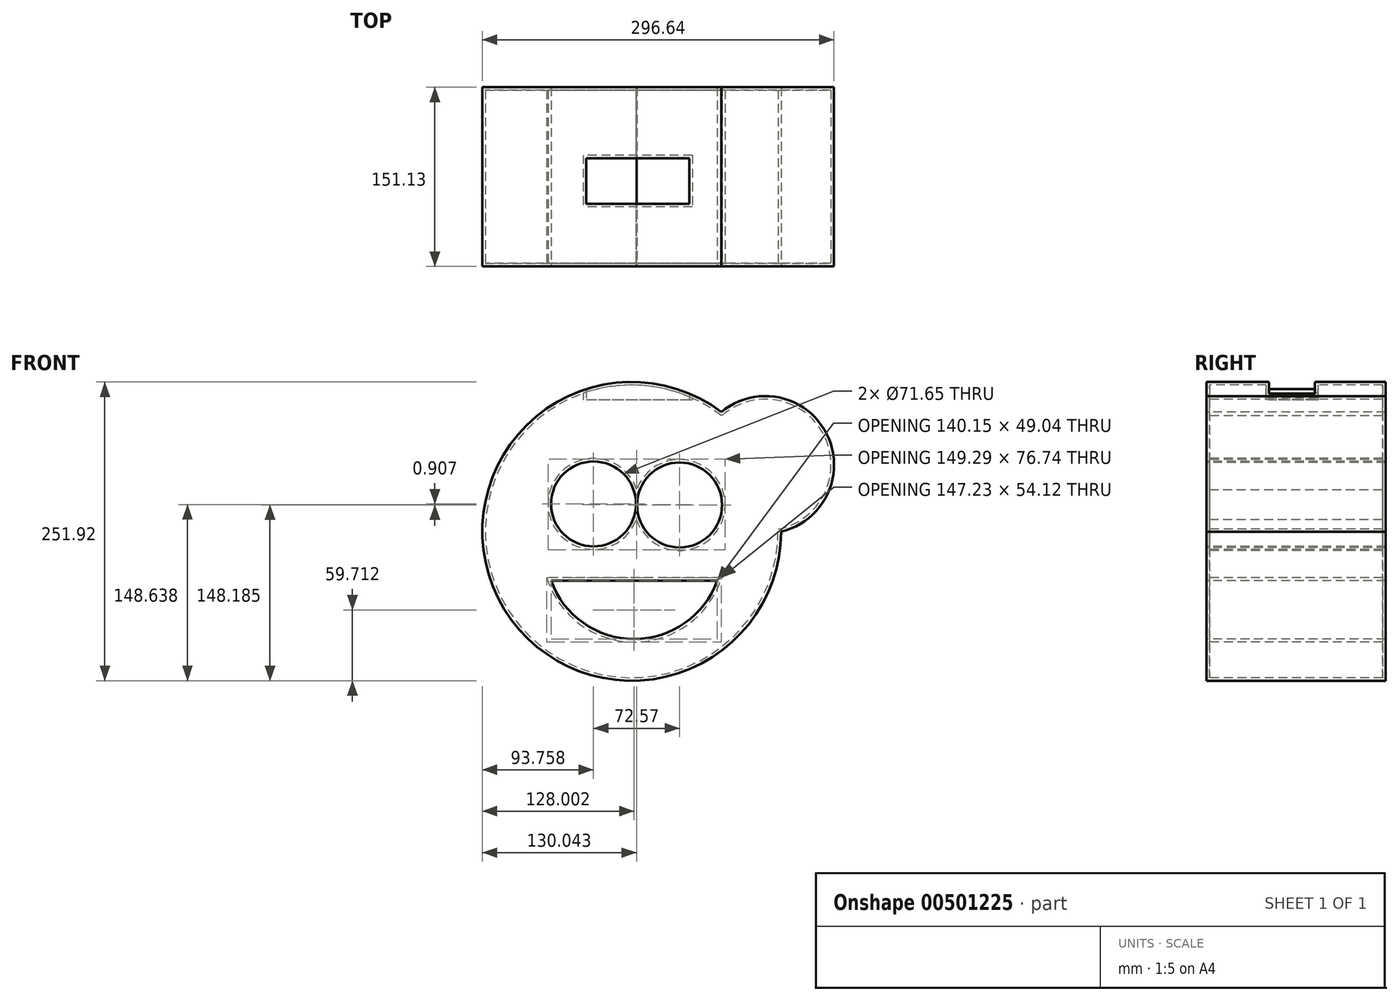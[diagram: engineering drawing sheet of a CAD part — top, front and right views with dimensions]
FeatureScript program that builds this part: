
annotation { "Feature Type Name" : "Feature", "Feature Type Description" : "" }
export const myFeature = defineFeature(function(context is Context, id is Id, definition is map)
    precondition{}
    {
        {
            var Q0;
            Q0=qCreatedBy(makeId("Front.planeOp"),FACE);
            var sketch = newSketch(context, id + "F0", { "sketchPlane" : qUnion([Q0])});
            skCircle(sketch, "E0", {"center": v(-37.2, 30.84) * mm, "radius": 35.83 * mm});
            skCircle(sketch, "E1", {"center": v(35.38, 29.93) * mm, "radius": 35.83 * mm});
            skCircle(sketch, "E2", {"center": v(-4.99, 7.71) * mm, "radius": 125.96 * mm});
            skLineSegment(sketch, "E3", {"start": v(67.13, -34.02) * mm, "end": v(-73.02, -34.02) * mm});
            skArc(sketch, "E4", {"start": v(-73.02, -34.02) * mm, "mid": v(-2.95, -83.06) * mm, "end": v(67.13, -34.02) * mm});
            skCircle(sketch, "E5", {"center": v(107.77, 63.86) * mm, "radius": 57.92 * mm});
            skSolve(sketch);
        }
        {
            var Q0;
            Q0 = qSketchRegion(id + "F0", true);
            extrude(context, id + "F1", {"entities" : qUnion([Q0]), "oppositeDirection" : true, "depth" : 151.13 * mm, "offsetDistance" : 25.4 * mm});
        }
        {
            var Q0;
            Q0=qCreatedBy(makeId("Top.planeOp"),FACE);
            cPlane(context, id + "F2", {"entities" : qUnion([Q0]), "cplaneType" : CPlaneType.OFFSET, "offset" : 118.62 * mm, "width" : 152.4 * mm, "height" : 152.4 * mm});
        }
        {
            var Q0;
            Q0=qCreatedBy(id+"F2.planeOp",FACE);
            var sketch = newSketch(context, id + "F3", { "sketchPlane" : qUnion([Q0])});
            skLineSegment(sketch, "E6.bottom", {"start": v(43.47, 91.3) * mm, "end": v(-43.47, 91.3) * mm});
            skLineSegment(sketch, "E6.top", {"start": v(43.47, 52.72) * mm, "end": v(-43.47, 52.72) * mm});
            skLineSegment(sketch, "E6.left", {"start": v(43.47, 91.3) * mm, "end": v(43.47, 52.72) * mm});
            skLineSegment(sketch, "E6.right", {"start": v(-43.47, 91.3) * mm, "end": v(-43.47, 52.72) * mm});
            skPoint(sketch, "E6.middle", {"position": v(0, 72.01) * mm});
            skSolve(sketch);
        }
        {
            var Q0;
            Q0 = qSketchRegion(id + "F3", true);
            extrude(context, id + "F4", {"entities" : qUnion([Q0]), "operationType" : NewBodyOperationType.REMOVE, "depth" : 44.96 * mm, "offsetDistance" : 25.4 * mm});
        }
        {
            var Q0;
            Q0=makeQuery(id+"F4.boolean.opBoolean","COPY",FACE,{"derivedFrom":makeQuery(id+"F4.opExtrude","CAP_FACE",FACE,{"disambiguationData":[OSD([sQuery(id+"F3.wireOp",EDGE,"E6.bottom"),sQuery(id+"F3.wireOp",EDGE,"E6.top"),sQuery(id+"F3.wireOp",EDGE,"E6.left"),sQuery(id+"F3.wireOp",EDGE,"E6.right")])],"isStart":true})});
            shell(context, id + "F5", {"entities" : qUnion([Q0]), "thickness" : 2.54 * mm});
        }
    });
